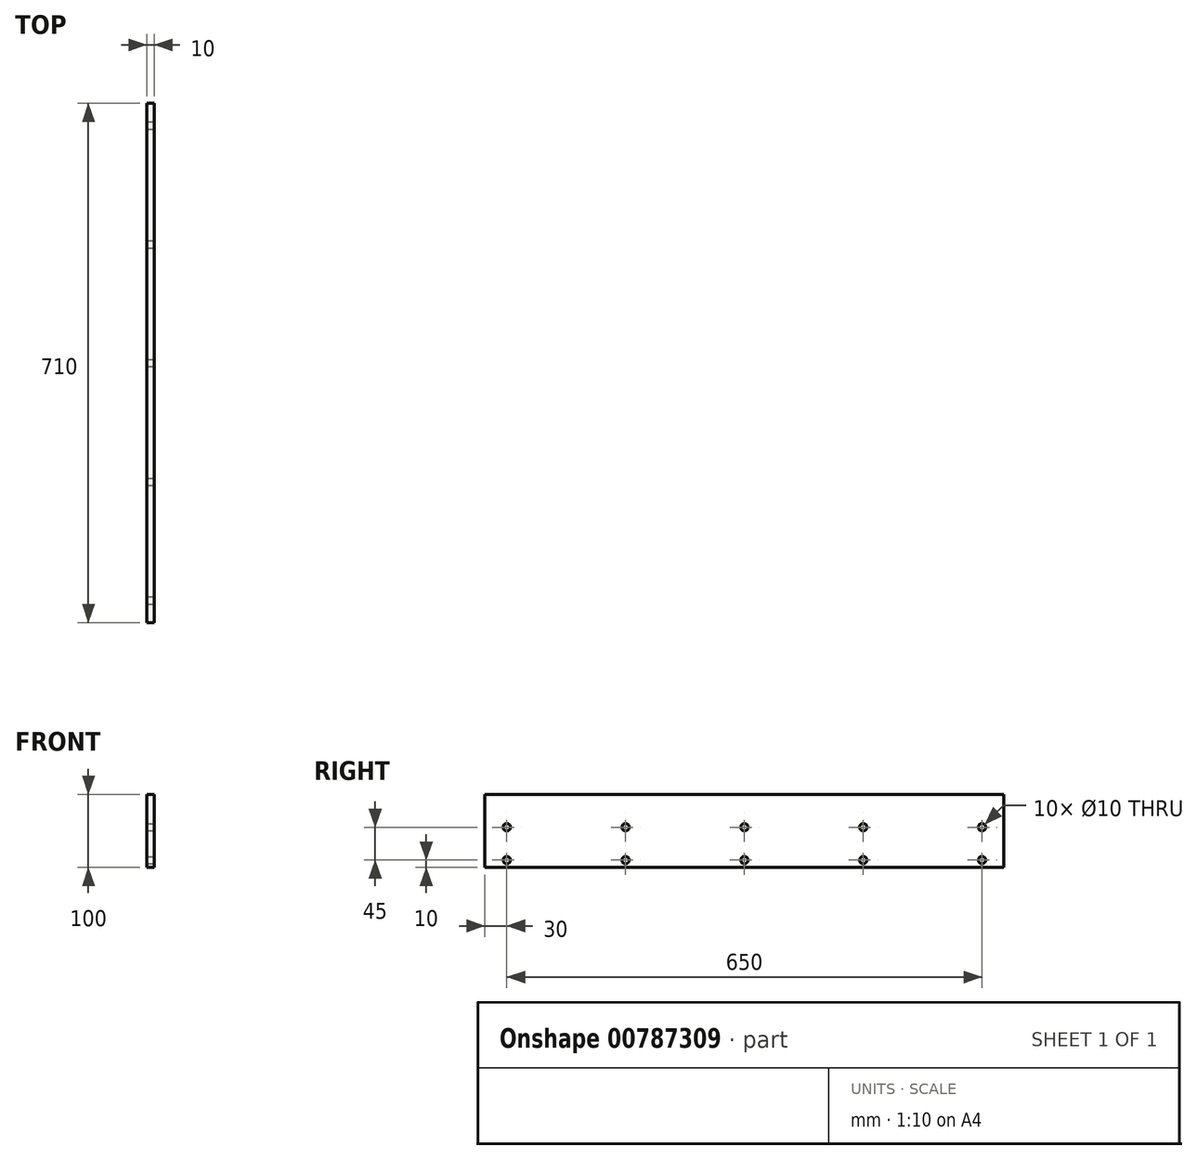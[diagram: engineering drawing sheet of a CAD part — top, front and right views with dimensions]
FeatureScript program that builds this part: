
annotation { "Feature Type Name" : "Feature", "Feature Type Description" : "" }
export const myFeature = defineFeature(function(context is Context, id is Id, definition is map)
    precondition{}
    {
        {
            var Q0;
            Q0=qCreatedBy(makeId("Front.planeOp"),FACE);
            var sketch = newSketch(context, id + "F0", { "sketchPlane" : qUnion([Q0])});
            skLineSegment(sketch, "E0.bottom", {"start": v(5, 50) * mm, "end": v(-5, 50) * mm});
            skLineSegment(sketch, "E0.top", {"start": v(5, -50) * mm, "end": v(-5, -50) * mm});
            skLineSegment(sketch, "E0.left", {"start": v(5, 50) * mm, "end": v(5, -50) * mm});
            skLineSegment(sketch, "E0.right", {"start": v(-5, 50) * mm, "end": v(-5, -50) * mm});
            skPoint(sketch, "E0.middle", {"position": v(0, 0) * mm});
            skSolve(sketch);
        }
        {
            var Q0;
            Q0=makeQuery(id+"F0.imprint","IMPRINT",FACE,{"disambiguationData":[TD([[makeQuery(id+"F0.imprint","IMPRINT",EDGE,{"derivedFrom":sQuery(id+"F0.wireOp",EDGE,"E0.bottom")}),1.0]])]});
            extrude(context, id + "F1", {"entities" : qUnion([Q0]), "depth" : 710 * mm, "offsetDistance" : 25 * mm});
        }
        {
            var Q0;
            Q0=makeQuery(id+"F1.opExtrude","SWEPT_FACE",FACE,{"disambiguationData":[OSD([sQuery(id+"F0.wireOp",EDGE,"E0.left")])]});
            var sketch = newSketch(context, id + "F2", { "sketchPlane" : qUnion([Q0])});
            skCircle(sketch, "E1", {"center": v(-680, 5) * mm, "radius": 5 * mm});
            skCircle(sketch, "E2", {"center": v(-680, -40) * mm, "radius": 5 * mm});
            skLineSegment(sketch, "E3", {"start": v(-355, 50) * mm, "end": v(-355, -50) * mm, "construction": true});
            skLineSegment(sketch, "E4", {"start": v(-680, 5) * mm, "end": v(-355, 5) * mm, "construction": true});
            skLineSegment(sketch, "E5", {"start": v(-680, -40) * mm, "end": v(-355, -40) * mm, "construction": true});
            skCircle(sketch, "E6", {"center": v(-355, 5) * mm, "radius": 5 * mm});
            skCircle(sketch, "E7", {"center": v(-355, -40) * mm, "radius": 5 * mm});
            skCircle(sketch, "E8", {"center": v(-517.5, 5) * mm, "radius": 5 * mm});
            skCircle(sketch, "E9", {"center": v(-517.5, -40) * mm, "radius": 5 * mm});
            skCircle(sketch, "E10.MirrorC", {"center": v(-192.5, -40) * mm, "radius": 5 * mm});
            skCircle(sketch, "E11.MirrorC", {"center": v(-192.5, 5) * mm, "radius": 5 * mm});
            skCircle(sketch, "E12.MirrorC", {"center": v(-30, 5) * mm, "radius": 5 * mm});
            skCircle(sketch, "E13.MirrorC", {"center": v(-30, -40) * mm, "radius": 5 * mm});
            skSolve(sketch);
        }
        {
            var Q0;
            Q0 = qSketchRegion(id + "F2", true);
            extrude(context, id + "F3", {"entities" : qUnion([Q0]), "operationType" : NewBodyOperationType.REMOVE, "oppositeDirection" : true, "depth" : 25 * mm, "offsetDistance" : 25 * mm});
        }
    });
